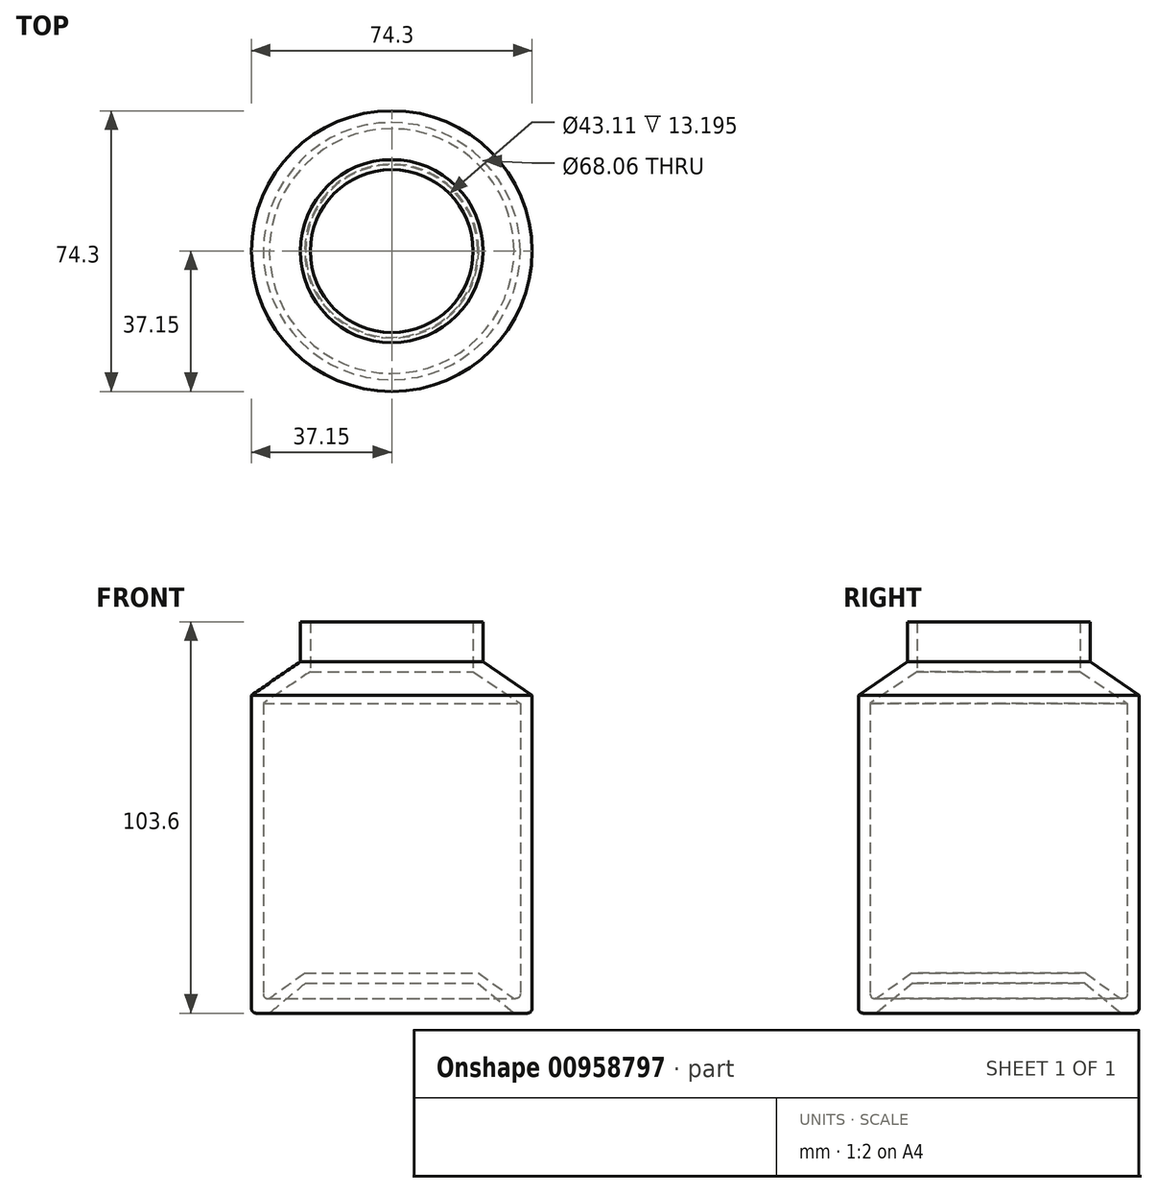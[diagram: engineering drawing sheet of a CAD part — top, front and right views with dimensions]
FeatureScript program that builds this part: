
annotation { "Feature Type Name" : "Feature", "Feature Type Description" : "" }
export const myFeature = defineFeature(function(context is Context, id is Id, definition is map)
    precondition{}
    {
        {
            var Q0;
            Q0=qCreatedBy(makeId("Front.planeOp"),FACE);
            var sketch = newSketch(context, id + "F0", { "sketchPlane" : qUnion([Q0])});
            skLineSegment(sketch, "E0", {"start": v(0, 0) * mm, "end": v(0, 83) * mm, "construction": true});
            skLineSegment(sketch, "E1", {"start": v(0, 0) * mm, "end": v(22.8, 0) * mm});
            skLineSegment(sketch, "E2", {"start": v(22.8, 0) * mm, "end": v(32.4, -7.96) * mm});
            skLineSegment(sketch, "E3", {"start": v(32.4, -7.96) * mm, "end": v(35.88, -7.96) * mm});
            skLineSegment(sketch, "E4", {"start": v(37.15, -6.69) * mm, "end": v(37.15, 76.21) * mm});
            skLineSegment(sketch, "E5", {"start": v(37.15, 76.21) * mm, "end": v(24.2, 85.09) * mm});
            skLineSegment(sketch, "E6", {"start": v(24.2, 85.09) * mm, "end": v(24.2, 95.64) * mm});
            skLineSegment(sketch, "E7", {"start": v(24.2, 95.64) * mm, "end": v(21.56, 95.64) * mm});
            skLineSegment(sketch, "E8", {"start": v(21.56, 95.64) * mm, "end": v(21.56, 82.45) * mm});
            skLineSegment(sketch, "E9", {"start": v(21.56, 82.45) * mm, "end": v(34.03, 74.05) * mm});
            skLineSegment(sketch, "E10", {"start": v(34.03, 74.05) * mm, "end": v(34.03, -2.85) * mm});
            skLineSegment(sketch, "E11", {"start": v(32.76, -4.12) * mm, "end": v(32.4, -4.12) * mm});
            skLineSegment(sketch, "E12", {"start": v(32.4, -4.12) * mm, "end": v(23.04, 2.6) * mm});
            skLineSegment(sketch, "E13", {"start": v(23.04, 2.6) * mm, "end": v(0, 2.6) * mm});
            skLineSegment(sketch, "E14", {"start": v(0, 2.6) * mm, "end": v(0, 0) * mm});
            skPoint(sketch, "E15.visualSharp", {"position": v(37.15, -7.96) * mm});
            skArc(sketch, "E15.filletArc", {"start": v(35.88, -7.96) * mm, "mid": v(36.78, -7.58) * mm, "end": v(37.15, -6.69) * mm});
            skPoint(sketch, "E16.visualSharp", {"position": v(34.03, -4.12) * mm});
            skArc(sketch, "E16.filletArc", {"start": v(32.76, -4.12) * mm, "mid": v(33.66, -3.74) * mm, "end": v(34.03, -2.85) * mm});
            skSolve(sketch);
        }
        {
            var Q0;
            Q0=makeQuery(id+"F0.imprint","IMPRINT",FACE,{"disambiguationData":[TD([[makeQuery(id+"F0.imprint","IMPRINT",EDGE,{"derivedFrom":sQuery(id+"F0.wireOp",EDGE,"E1")}),1.0]])]});
            var Q1;
            Q1=sQuery(id+"F0.wireOp",EDGE,"E0");
            revolve(context, id + "F1", {"surfaceOperationType" : NewSurfaceOperationType.NEW, "entities" : qUnion([Q0]), "axis" : qUnion([Q1]), "revolveType" : RevolveType.FULL});
        }
    });
